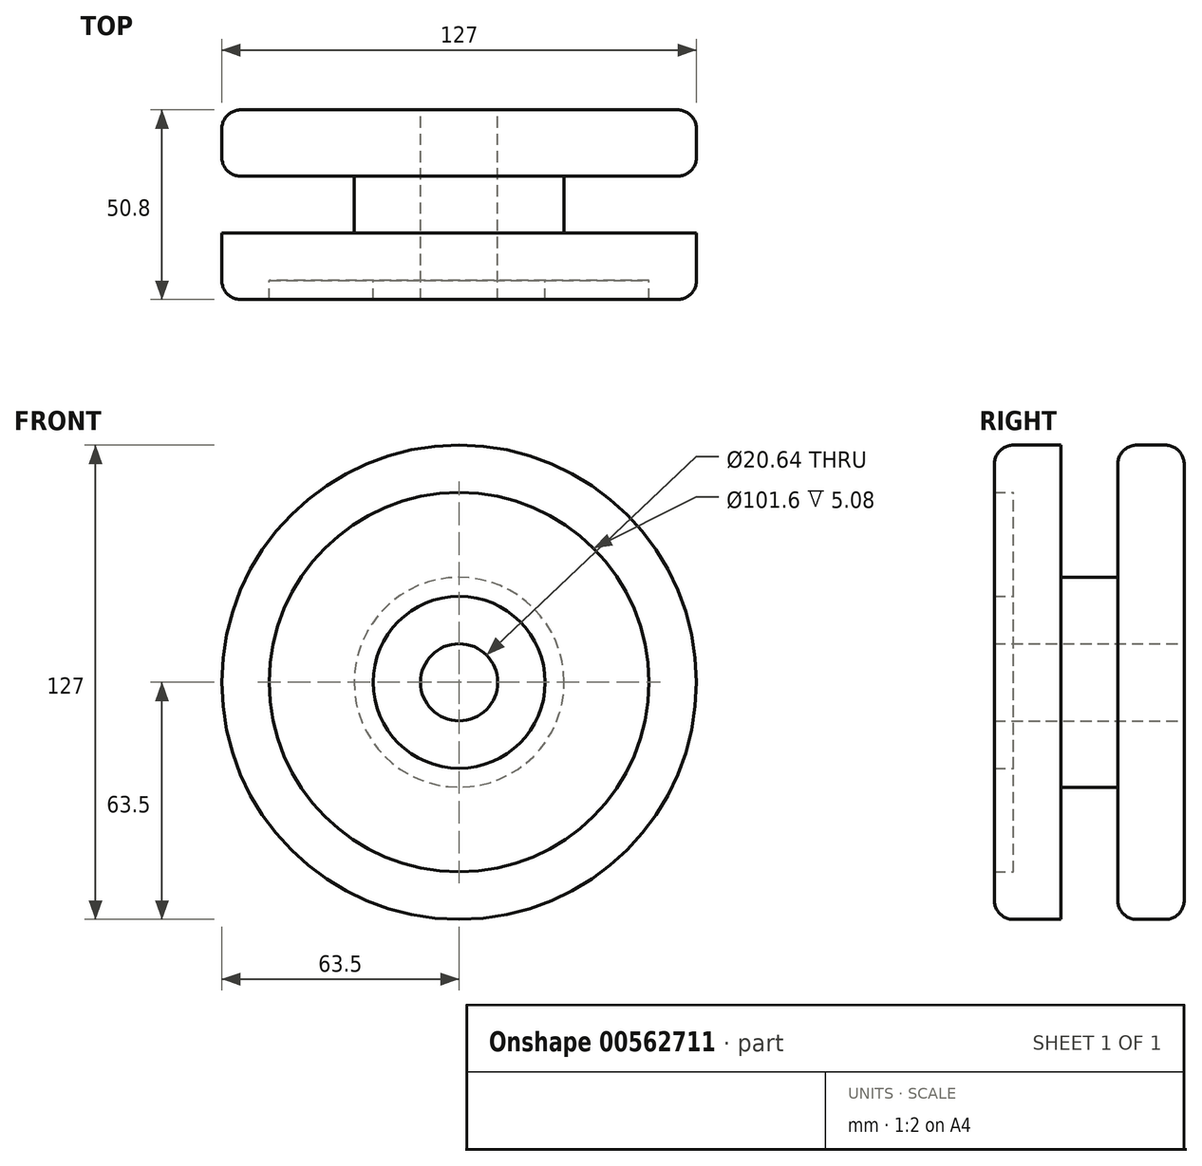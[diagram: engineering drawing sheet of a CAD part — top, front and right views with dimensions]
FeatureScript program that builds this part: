
annotation { "Feature Type Name" : "Feature", "Feature Type Description" : "" }
export const myFeature = defineFeature(function(context is Context, id is Id, definition is map)
    precondition{}
    {
        {
            var Q0;
            Q0=qCreatedBy(makeId("Front.planeOp"),FACE);
            var sketch = newSketch(context, id + "F0", { "sketchPlane" : qUnion([Q0])});
            skCircle(sketch, "E0", {"center": v(0, 0) * mm, "radius": 63.5 * mm});
            skCircle(sketch, "E1", {"center": v(0, 0) * mm, "radius": 10.32 * mm});
            skSolve(sketch);
        }
        {
            var Q0;
            Q0=makeQuery(id+"F0.imprint","IMPRINT",FACE,{"disambiguationData":[TD([[makeQuery(id+"F0.imprint","IMPRINT",EDGE,{"derivedFrom":sQuery(id+"F0.wireOp",EDGE,"E0")}),1.0]])]});
            extrude(context, id + "F1", {"entities" : qUnion([Q0]), "endBound" : BoundingType.SYMMETRIC, "depth" : 50.8 * mm, "offsetDistance" : 25.4 * mm});
        }
        {
            var Q0;
            Q0=makeQuery(id+"F1.opExtrude","SWEPT_FACE",FACE,{"disambiguationData":[OSD([sQuery(id+"F0.wireOp",EDGE,"E0")])]});
            shell(context, id + "F2", {"entities" : qUnion([Q0]), "thickness" : 17.78 * mm});
        }
        {
            var Q0;
            Q0=makeQuery(id+"F2.opShell","OFFSET_FACE",FACE,{"disambiguationData":[OSD([sQuery(id+"F0.wireOp",EDGE,"E0")])]});
            var Q1;
            Q1=makeQuery(id+"F1.opExtrude","CAP_EDGE",EDGE,{"disambiguationData":[OSD([sQuery(id+"F0.wireOp",EDGE,"E0")])],"isStart":false});
            fillet(context, id + "F3", {"entities" : qUnion([Q0, Q1]), "radius" : 5.08 * mm, "tangentPropagation" : true, "allowEdgeOverflow" : false});
        }
        {
            var Q0;
            Q0=makeQuery(id+"F1.opExtrude","CAP_FACE",FACE,{"disambiguationData":[OSD([sQuery(id+"F0.wireOp",EDGE,"E0"),sQuery(id+"F0.wireOp",EDGE,"E1")])],"isStart":false});
            shell(context, id + "F4", {"entities" : qUnion([Q0]), "thickness" : 12.7 * mm});
        }
    });
